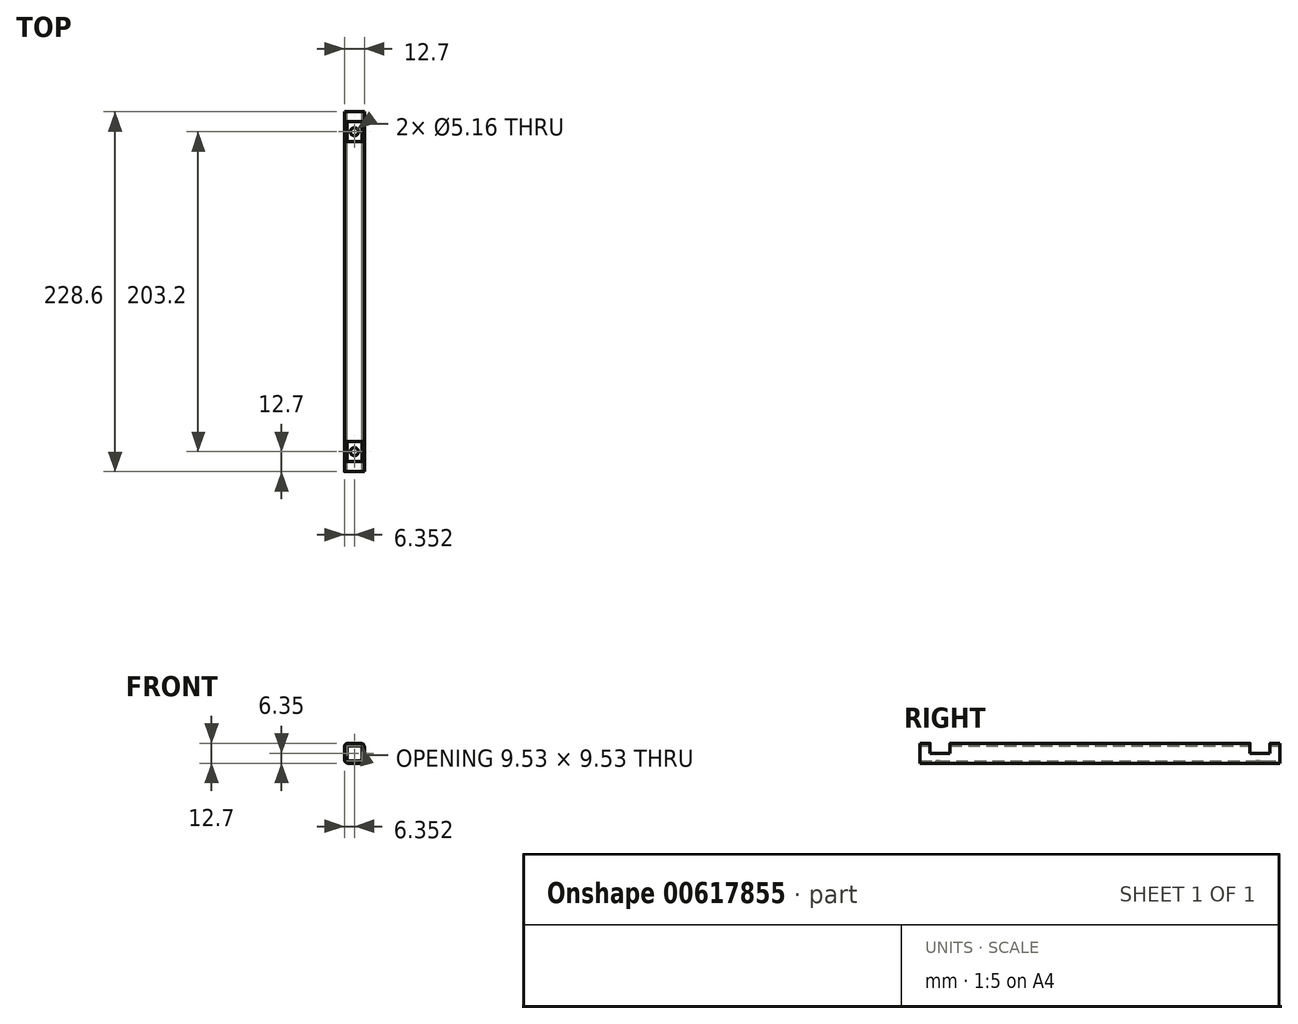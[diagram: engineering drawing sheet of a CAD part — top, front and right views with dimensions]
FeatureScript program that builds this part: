
annotation { "Feature Type Name" : "Feature", "Feature Type Description" : "" }
export const myFeature = defineFeature(function(context is Context, id is Id, definition is map)
    precondition{}
    {
        {
            var Q0;
            Q0=qCreatedBy(makeId("Front.planeOp"),FACE);
            var sketch = newSketch(context, id + "F0", { "sketchPlane" : qUnion([Q0])});
            skLineSegment(sketch, "E0.bottom", {"start": v(7.7, 0) * mm, "end": v(-0.25, 0) * mm});
            skLineSegment(sketch, "E0.top", {"start": v(7.7, -12.7) * mm, "end": v(-0.25, -12.7) * mm});
            skLineSegment(sketch, "E0.left", {"start": v(10.07, -2.38) * mm, "end": v(10.07, -10.32) * mm});
            skLineSegment(sketch, "E0.right", {"start": v(-2.63, -2.38) * mm, "end": v(-2.63, -10.32) * mm});
            skPoint(sketch, "E0.middle", {"position": v(3.72, -6.35) * mm});
            skPoint(sketch, "E1.visualSharp", {"position": v(-2.63, 0) * mm});
            skArc(sketch, "E1.filletArc", {"start": v(-0.25, 0) * mm, "mid": v(-1.93, -0.7) * mm, "end": v(-2.63, -2.38) * mm});
            skPoint(sketch, "E2.visualSharp", {"position": v(-2.63, -12.7) * mm});
            skArc(sketch, "E2.filletArc", {"start": v(-2.63, -10.32) * mm, "mid": v(-1.93, -12) * mm, "end": v(-0.25, -12.7) * mm});
            skPoint(sketch, "E3.visualSharp", {"position": v(10.07, -12.7) * mm});
            skArc(sketch, "E3.filletArc", {"start": v(7.7, -12.7) * mm, "mid": v(9.37, -12) * mm, "end": v(10.07, -10.32) * mm});
            skPoint(sketch, "E4.visualSharp", {"position": v(10.07, 0) * mm});
            skArc(sketch, "E4.filletArc", {"start": v(10.07, -2.38) * mm, "mid": v(9.37, -0.7) * mm, "end": v(7.7, 0) * mm});
            skLineSegment(sketch, "E5.bottom", {"start": v(6.9, -1.59) * mm, "end": v(0.55, -1.59) * mm});
            skLineSegment(sketch, "E5.top", {"start": v(6.9, -11.11) * mm, "end": v(0.55, -11.11) * mm});
            skLineSegment(sketch, "E5.left", {"start": v(8.48, -3.17) * mm, "end": v(8.48, -9.53) * mm});
            skLineSegment(sketch, "E5.right", {"start": v(-1.04, -3.18) * mm, "end": v(-1.04, -9.53) * mm});
            skPoint(sketch, "E6.visualSharp", {"position": v(-1.04, -1.59) * mm});
            skArc(sketch, "E6.filletArc", {"start": v(0.55, -1.59) * mm, "mid": v(-0.58, -2.05) * mm, "end": v(-1.04, -3.18) * mm});
            skPoint(sketch, "E7.visualSharp", {"position": v(8.48, -1.59) * mm});
            skArc(sketch, "E7.filletArc", {"start": v(8.48, -3.17) * mm, "mid": v(8.02, -2.05) * mm, "end": v(6.9, -1.59) * mm});
            skPoint(sketch, "E8.visualSharp", {"position": v(8.48, -11.11) * mm});
            skArc(sketch, "E8.filletArc", {"start": v(6.9, -11.11) * mm, "mid": v(8.02, -10.65) * mm, "end": v(8.48, -9.53) * mm});
            skPoint(sketch, "E9.visualSharp", {"position": v(-1.04, -11.11) * mm});
            skArc(sketch, "E9.filletArc", {"start": v(-1.04, -9.53) * mm, "mid": v(-0.58, -10.65) * mm, "end": v(0.55, -11.11) * mm});
            skSolve(sketch);
        }
        {
            var Q0;
            Q0=qSketchRegion(id+"F0",true);
            extrude(context, id + "F1", {"entities" : qUnion([Q0]), "depth" : 228.6 * mm, "offsetDistance" : 25.4 * mm});
        }
        {
            var Q0;
            Q0=qCreatedBy(makeId("Right.planeOp"),FACE);
            var sketch = newSketch(context, id + "F2", { "sketchPlane" : qUnion([Q0])});
            skLineSegment(sketch, "E10.bottom", {"start": v(-222.25, 0) * mm, "end": v(-209.55, 0) * mm});
            skLineSegment(sketch, "E10.top", {"start": v(-222.25, -6.35) * mm, "end": v(-209.55, -6.35) * mm});
            skLineSegment(sketch, "E10.left", {"start": v(-222.25, 0) * mm, "end": v(-222.25, -6.35) * mm});
            skLineSegment(sketch, "E10.right", {"start": v(-209.55, 0) * mm, "end": v(-209.55, -6.35) * mm});
            skLineSegment(sketch, "E11.bottom", {"start": v(-6.35, 0) * mm, "end": v(-19.05, 0) * mm});
            skLineSegment(sketch, "E11.top", {"start": v(-6.35, -6.35) * mm, "end": v(-19.05, -6.35) * mm});
            skLineSegment(sketch, "E11.left", {"start": v(-6.35, 0) * mm, "end": v(-6.35, -6.35) * mm});
            skLineSegment(sketch, "E11.right", {"start": v(-19.05, 0) * mm, "end": v(-19.05, -6.35) * mm});
            skSolve(sketch);
        }
        {
            var Q0;
            Q0=qSketchRegion(id+"F2",true);
            extrude(context, id + "F3", {"entities" : qUnion([Q0]), "operationType" : NewBodyOperationType.REMOVE, "depth" : 11.94 * mm, "offsetDistance" : 25.4 * mm, "hasSecondDirection" : true, "secondDirectionOppositeDirection" : true, "secondDirectionDepth" : 25.4 * mm});
        }
        {
            var Q0;
            Q0=qCreatedBy(makeId("Top.planeOp"),FACE);
            var sketch = newSketch(context, id + "F4", { "sketchPlane" : qUnion([Q0])});
            skCircle(sketch, "E12", {"center": v(3.72, -12.7) * mm, "radius": 2.58 * mm});
            skCircle(sketch, "E13", {"center": v(3.72, -215.9) * mm, "radius": 2.58 * mm});
            skSolve(sketch);
        }
        {
            var Q0;
            Q0 = qSketchRegion(id + "F4", true);
            extrude(context, id + "F5", {"entities" : qUnion([Q0]), "operationType" : NewBodyOperationType.REMOVE, "oppositeDirection" : true, "depth" : 12.7 * mm, "offsetDistance" : 25.4 * mm});
        }
    });
